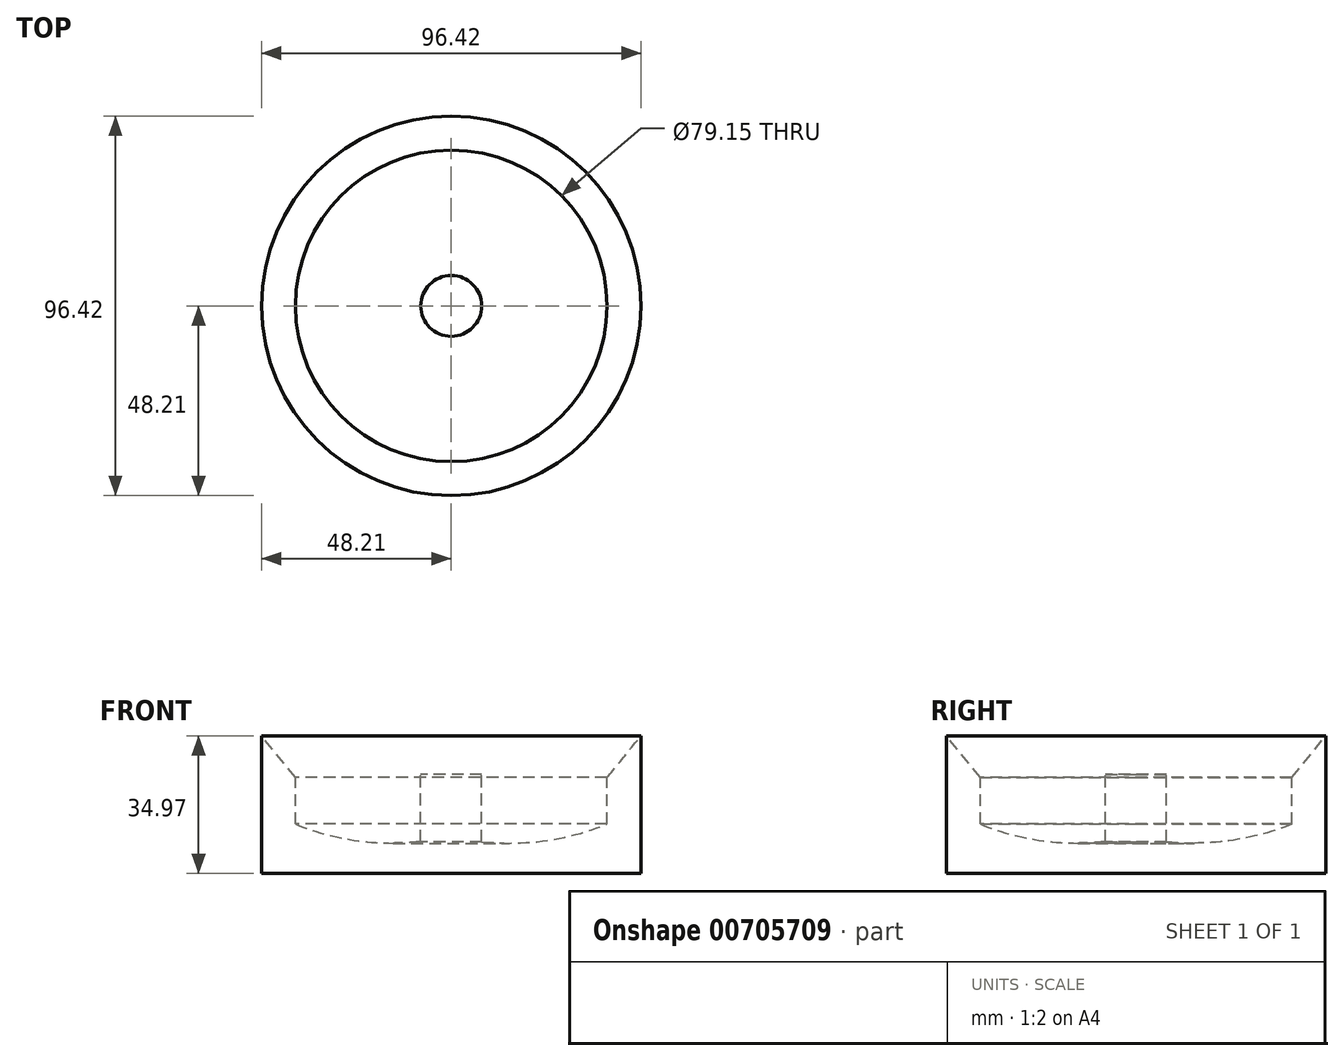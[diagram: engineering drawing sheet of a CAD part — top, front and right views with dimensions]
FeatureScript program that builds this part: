
annotation { "Feature Type Name" : "Feature", "Feature Type Description" : "" }
export const myFeature = defineFeature(function(context is Context, id is Id, definition is map)
    precondition{}
    {
        {
            var Q0;
            Q0=qCreatedBy(makeId("Front.planeOp"),FACE);
            var sketch = newSketch(context, id + "F0", { "sketchPlane" : qUnion([Q0])});
            skLineSegment(sketch, "E0.bottom", {"start": v(-48.2, 0) * mm, "end": v(0, 0) * mm});
            skLineSegment(sketch, "E0.left", {"start": v(-48.2, 0) * mm, "end": v(-48.2, 12.52) * mm});
            skLineSegment(sketch, "E1.left", {"start": v(-48.2, 12.52) * mm, "end": v(-48.2, 24.32) * mm});
            skLineSegment(sketch, "E1.right", {"start": v(-39.57, 12.52) * mm, "end": v(-39.57, 24.32) * mm});
            skArc(sketch, "E2", {"start": v(-39.57, 12.52) * mm, "mid": v(-23.93, 8.32) * mm, "end": v(-7.74, 8.06) * mm});
            skLineSegment(sketch, "E3", {"start": v(0, 9.35) * mm, "end": v(0, 0) * mm});
            skLineSegment(sketch, "E4", {"start": v(-7.74, 8.06) * mm, "end": v(-7.74, 25.19) * mm});
            skLineSegment(sketch, "E5", {"start": v(-7.74, 25.19) * mm, "end": v(0, 25.19) * mm});
            skLineSegment(sketch, "E6", {"start": v(0, 25.19) * mm, "end": v(0, 9.35) * mm});
            skLineSegment(sketch, "E7", {"start": v(-48.2, 24.32) * mm, "end": v(-48.2, 34.97) * mm});
            skLineSegment(sketch, "E8", {"start": v(-48.2, 34.97) * mm, "end": v(-39.57, 24.32) * mm});
            skSolve(sketch);
        }
        {
            var Q0;
            Q0 = qSketchRegion(id + "F0", true);
            var Q1;
            Q1=sQuery(id+"F0.wireOp",EDGE,"E6");
            revolve(context, id + "F1", {"surfaceOperationType" : NewSurfaceOperationType.NEW, "entities" : qUnion([Q0]), "axis" : qUnion([Q1]), "revolveType" : RevolveType.FULL});
        }
    });
